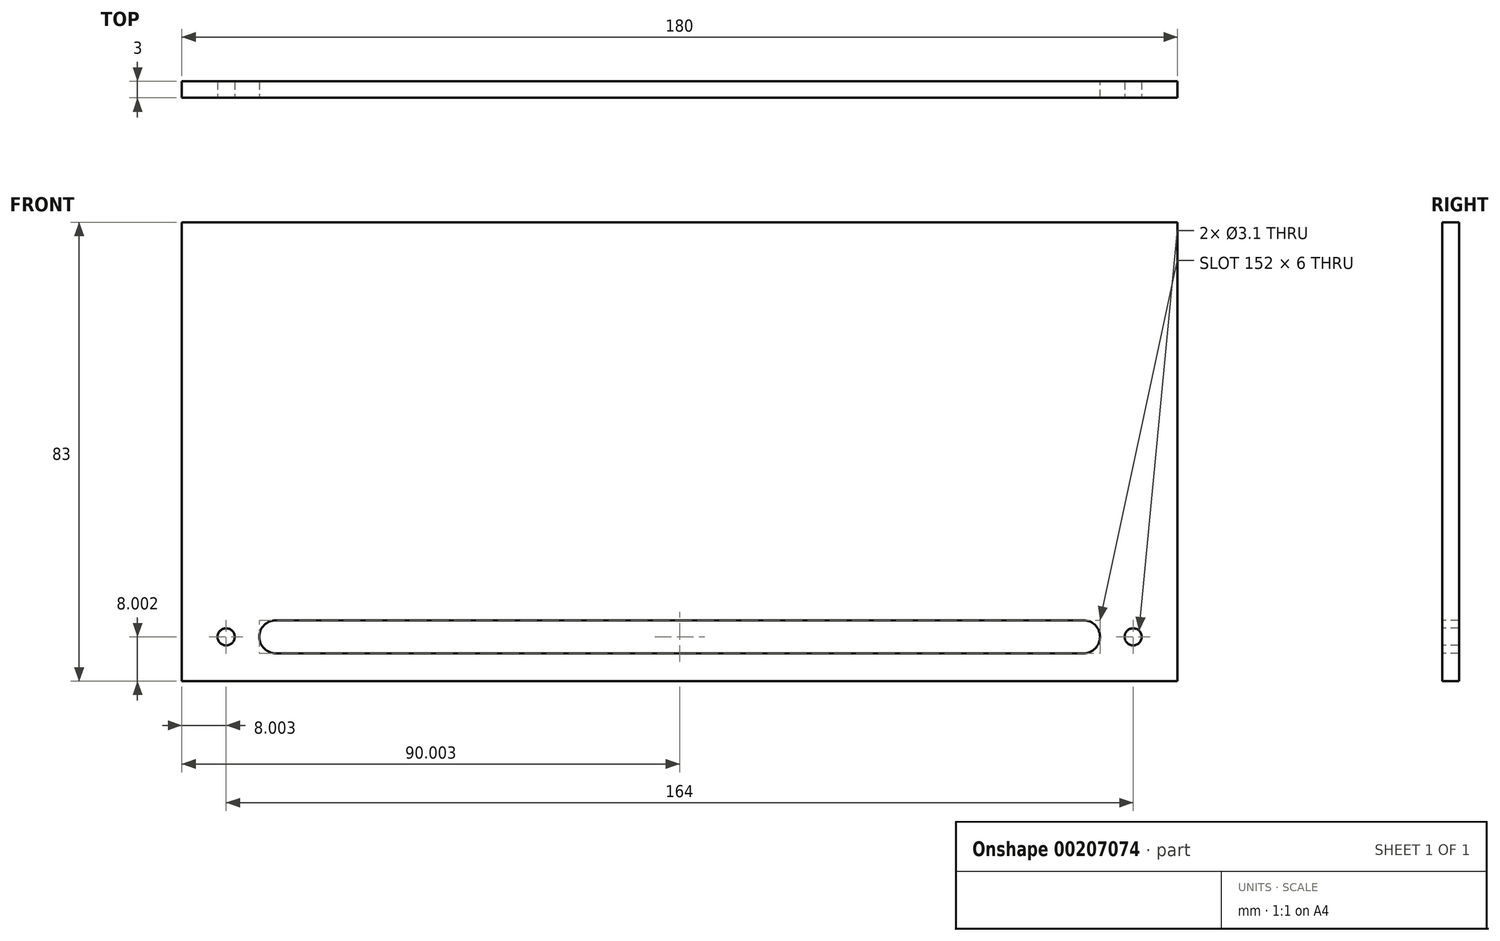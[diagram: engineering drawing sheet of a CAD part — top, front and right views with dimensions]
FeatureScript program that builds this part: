
annotation { "Feature Type Name" : "Feature", "Feature Type Description" : "" }
export const myFeature = defineFeature(function(context is Context, id is Id, definition is map)
    precondition{}
    {
        {
            var Q0;
            Q0=qCreatedBy(makeId("Front.planeOp"),FACE);
            var sketch = newSketch(context, id + "F0", { "sketchPlane" : qUnion([Q0])});
            skLineSegment(sketch, "E0.bottom", {"start": v(9, 100.35) * mm, "end": v(189, 100.35) * mm});
            skLineSegment(sketch, "E0.top", {"start": v(9, 17.35) * mm, "end": v(189, 17.35) * mm});
            skLineSegment(sketch, "E0.left", {"start": v(9, 100.35) * mm, "end": v(9, 17.35) * mm});
            skLineSegment(sketch, "E0.right", {"start": v(189, 100.35) * mm, "end": v(189, 17.35) * mm});
            skSolve(sketch);
        }
        {
            var Q0;
            Q0=makeQuery(id+"F0.imprint","IMPRINT",FACE,{"disambiguationData":[TD([[makeQuery(id+"F0.imprint","IMPRINT",EDGE,{"derivedFrom":sQuery(id+"F0.wireOp",EDGE,"E0.bottom")}),-1.0]])]});
            extrude(context, id + "F1", {"entities" : qUnion([Q0]), "depth" : 3 * mm});
        }
        {
            var Q0;
            Q0=makeQuery(id+"F1.opExtrude","CAP_FACE",FACE,{"disambiguationData":[OSD([sQuery(id+"F0.wireOp",EDGE,"E0.bottom"),sQuery(id+"F0.wireOp",EDGE,"E0.top"),sQuery(id+"F0.wireOp",EDGE,"E0.left"),sQuery(id+"F0.wireOp",EDGE,"E0.right")])],"isStart":false});
            var sketch = newSketch(context, id + "F2", { "sketchPlane" : qUnion([Q0])});
            skLineSegment(sketch, "E1", {"start": v(189, 25.35) * mm, "end": v(181, 25.35) * mm, "construction": true});
            skCircle(sketch, "E2", {"center": v(181, 25.35) * mm, "radius": 1.55 * mm});
            skLineSegment(sketch, "E3.bottom", {"start": v(175, 22.35) * mm, "end": v(23, 22.35) * mm});
            skLineSegment(sketch, "E3.top", {"start": v(175, 28.35) * mm, "end": v(23, 28.35) * mm});
            skLineSegment(sketch, "E3.left", {"start": v(175, 22.35) * mm, "end": v(175, 28.35) * mm});
            skLineSegment(sketch, "E3.right", {"start": v(23, 22.35) * mm, "end": v(23, 28.35) * mm});
            skLineSegment(sketch, "E4", {"start": v(17, 17.35) * mm, "end": v(17, 25.35) * mm, "construction": true});
            skCircle(sketch, "E5", {"center": v(17, 25.35) * mm, "radius": 1.55 * mm});
            skSolve(sketch);
        }
        {
            var Q0;
            Q0 = qSketchRegion(id + "F2", true);
            extrude(context, id + "F3", {"entities" : qUnion([Q0]), "operationType" : NewBodyOperationType.REMOVE, "oppositeDirection" : true, "depth" : 25 * mm});
        }
        {
            var Q0;
            Q0=makeQuery(id+"F3.boolean.opBoolean","COPY",EDGE,{"derivedFrom":makeQuery(id+"F3.opExtrude","SWEPT_EDGE",EDGE,{"disambiguationData":[OSD([sQuery(id+"F2.wireOp",EDGE,"E3.top"),sQuery(id+"F2.wireOp",EDGE,"E3.right")])]})});
            var Q1;
            Q1=makeQuery(id+"F3.boolean.opBoolean","COPY",EDGE,{"derivedFrom":makeQuery(id+"F3.opExtrude","SWEPT_EDGE",EDGE,{"disambiguationData":[OSD([sQuery(id+"F2.wireOp",EDGE,"E3.bottom"),sQuery(id+"F2.wireOp",EDGE,"E3.right")])]})});
            var Q2;
            Q2=makeQuery(id+"F3.boolean.opBoolean","COPY",EDGE,{"derivedFrom":makeQuery(id+"F3.opExtrude","SWEPT_EDGE",EDGE,{"disambiguationData":[OSD([sQuery(id+"F2.wireOp",EDGE,"E3.top"),sQuery(id+"F2.wireOp",EDGE,"E3.left")])]})});
            var Q3;
            Q3=makeQuery(id+"F3.boolean.opBoolean","COPY",EDGE,{"derivedFrom":makeQuery(id+"F3.opExtrude","SWEPT_EDGE",EDGE,{"disambiguationData":[OSD([sQuery(id+"F2.wireOp",EDGE,"E3.bottom"),sQuery(id+"F2.wireOp",EDGE,"E3.left")])]})});
            fillet(context, id + "F4", {"entities" : qUnion([Q0, Q1, Q2, Q3]), "radius" : 3 * mm, "tangentPropagation" : true, "allowEdgeOverflow" : false});
        }
    });
